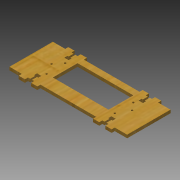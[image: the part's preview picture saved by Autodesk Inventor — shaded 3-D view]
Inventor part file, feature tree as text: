
AUTODESK INVENTOR PART (.ipt)
format: ipt  version: 2014 (Build 180170000, 170)  size: 285,696 bytes
history: native  units: mm
features: extrude x12, sketch x3
ambient origin geometry x8: Origin, YZ Plane, XZ Plane, XY Plane, X Axis, Y Axis, Z Axis, Center Point
bodies: Body1 (feature_tree)
feature tree (15):
  extrude  "Extrusion3"  Depth=70.0mm
  sketch  "Sketch3"  dims[d0=190.0mm d1=70.0mm]
  extrude  "Extrusion4"  Depth=5.0mm
  extrude  "Extrusion5"  Depth=3.5mm
  extrude  "Extrusion9"  Depth=3.5mm
  extrude  "Extrusion10"  Depth=5.0mm
  extrude  "Extrusion11"  Depth=2.0mm
  extrude  "Extrusion12"  Depth=2.0mm
  extrude  "Extrusion17"  Depth=40.0mm
  extrude  "Extrusion18"  Depth=8.0mm
  extrude  "Extrusion19"  Depth=13.0mm
  extrude  "Extrusion20"  Depth=40.0mm
  extrude  "Extrusion22"  Depth=13.0mm
  sketch  "Sketch4"  dims[d12=5.0mm d13=0.0mm d14=35.0mm]
  sketch  "Sketch5"  dims[d15=13.0mm d16=3.5mm d17=3.5mm d18=5.0mm d19=2.0mm d20=2.0mm d21=40.0mm d22=13.0mm d23=3.5mm d24=3.5mm d25=5.0mm d26=2.0mm d27=2.0mm d28=40.0mm d29=8.0mm d30=13.0mm d31=40.0mm d32=13.0mm d33=3.5mm d34=5.0mm d35=2.0mm d36=3.5mm d37=5.0mm d38=2.0mm d39=40.0mm d40=13.0mm d41=3.5mm d42=5.0mm d43=2.0mm d44=3.5mm d45=5.0mm d46=2.0mm d47=5.0mm d48=0.0mm d49=5.0mm d50=0.0mm d57=5.0mm d58=0.0mm d59=5.0mm d60=0.0mm d63=8.0mm d66=1.5mm d67=5.0mm d68=1.5mm d69=2.0mm d70=5.0mm d71=1.5mm d72=2.0mm d73=8.0mm d74=2.0mm d75=1.5mm d76=5.0mm d77=0.0mm d78=5.0mm d79=0.0mm d88=5.0mm d89=0.0mm d90=20.0mm d91=5.0mm d92=10.0mm d93=10.0mm d94=10.0mm d95=190.0mm d96=20.0mm d97=10.0mm d98=10.0mm d99=10.0mm d100=5.0mm d101=0.0mm d102=20.0mm d103=5.0mm d104=10.0mm d105=10.0mm d106=10.0mm d107=190.0mm d108=20.0mm d109=5.0mm d110=10.0mm d111=10.0mm d112=5.0mm d113=10.0mm d114=5.0mm d115=0.0mm d116=40.0mm d118=50.0mm d119=40.0mm d120=90.0mm d121=10.0mm d122=0.0mm d125=3.0mm d126=3.0mm d127=3.0mm d128=3.0mm d130=20.0mm d131=20.0mm d132=20.0mm d133=3.0mm d134=3.0mm d137=10.0mm d138=0.0mm d140=20.0mm d141=20.0mm d145=18.0mm d146=18.0mm]
